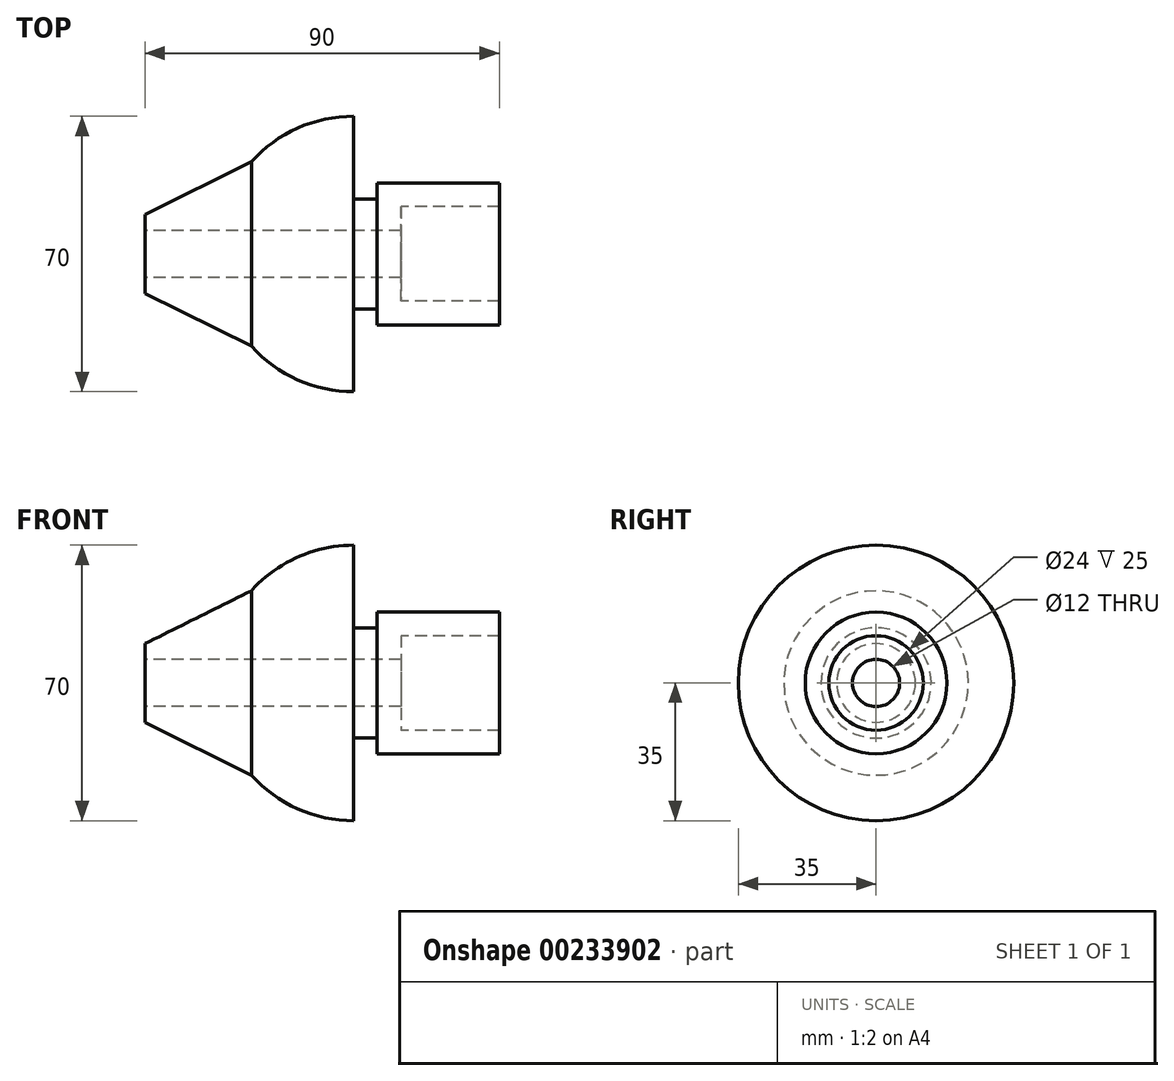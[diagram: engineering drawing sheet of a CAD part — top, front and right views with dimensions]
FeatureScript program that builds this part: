
annotation { "Feature Type Name" : "Feature", "Feature Type Description" : "" }
export const myFeature = defineFeature(function(context is Context, id is Id, definition is map)
    precondition{}
    {
        {
            var Q0;
            Q0=qCreatedBy(makeId("Front.planeOp"),FACE);
            var sketch = newSketch(context, id + "F0", { "sketchPlane" : qUnion([Q0])});
            skLineSegment(sketch, "E0", {"start": v(-78, 0) * mm, "end": v(77.4, 0) * mm});
            skLineSegment(sketch, "E1", {"start": v(46.8, 0) * mm, "end": v(46.8, 18) * mm});
            skLineSegment(sketch, "E2", {"start": v(46.8, 18) * mm, "end": v(15.8, 18) * mm});
            skLineSegment(sketch, "E3", {"start": v(15.8, 18) * mm, "end": v(15.8, 14) * mm});
            skLineSegment(sketch, "E4", {"start": v(15.8, 14) * mm, "end": v(9.8, 14) * mm});
            skLineSegment(sketch, "E5", {"start": v(9.8, 14) * mm, "end": v(9.8, 35) * mm});
            skLineSegment(sketch, "E6", {"start": v(46.8, 12) * mm, "end": v(21.8, 12) * mm});
            skLineSegment(sketch, "E7", {"start": v(21.8, 12) * mm, "end": v(21.8, 0) * mm});
            skLineSegment(sketch, "E8", {"start": v(-43.2, 6) * mm, "end": v(21.8, 6) * mm});
            skLineSegment(sketch, "E9", {"start": v(-43.2, 0) * mm, "end": v(-43.2, 10) * mm});
            skArc(sketch, "E10", {"start": v(9.8, 35) * mm, "mid": v(-4.43, 31.98) * mm, "end": v(-16.2, 23.43) * mm});
            skLineSegment(sketch, "E11", {"start": v(-43.2, 10) * mm, "end": v(-16.2, 23.43) * mm});
            skSolve(sketch);
        }
        {
            var Q0;
            {var subQ4=sQuery(id+"F0.wireOp",EDGE,"E2");Q0=makeQuery(id+"F0.imprint","IMPRINT",FACE,{"disambiguationData":[TD([[makeQuery(id+"F0.imprint","IMPRINT",EDGE,{"derivedFrom":subQ4}),1.0]])]});}
            var Q1;
            Q1=sQuery(id+"F0.wireOp",EDGE,"E0");
            revolve(context, id + "F1", {"entities" : qUnion([Q0]), "axis" : qUnion([Q1]), "revolveType" : RevolveType.FULL});
        }
    });
